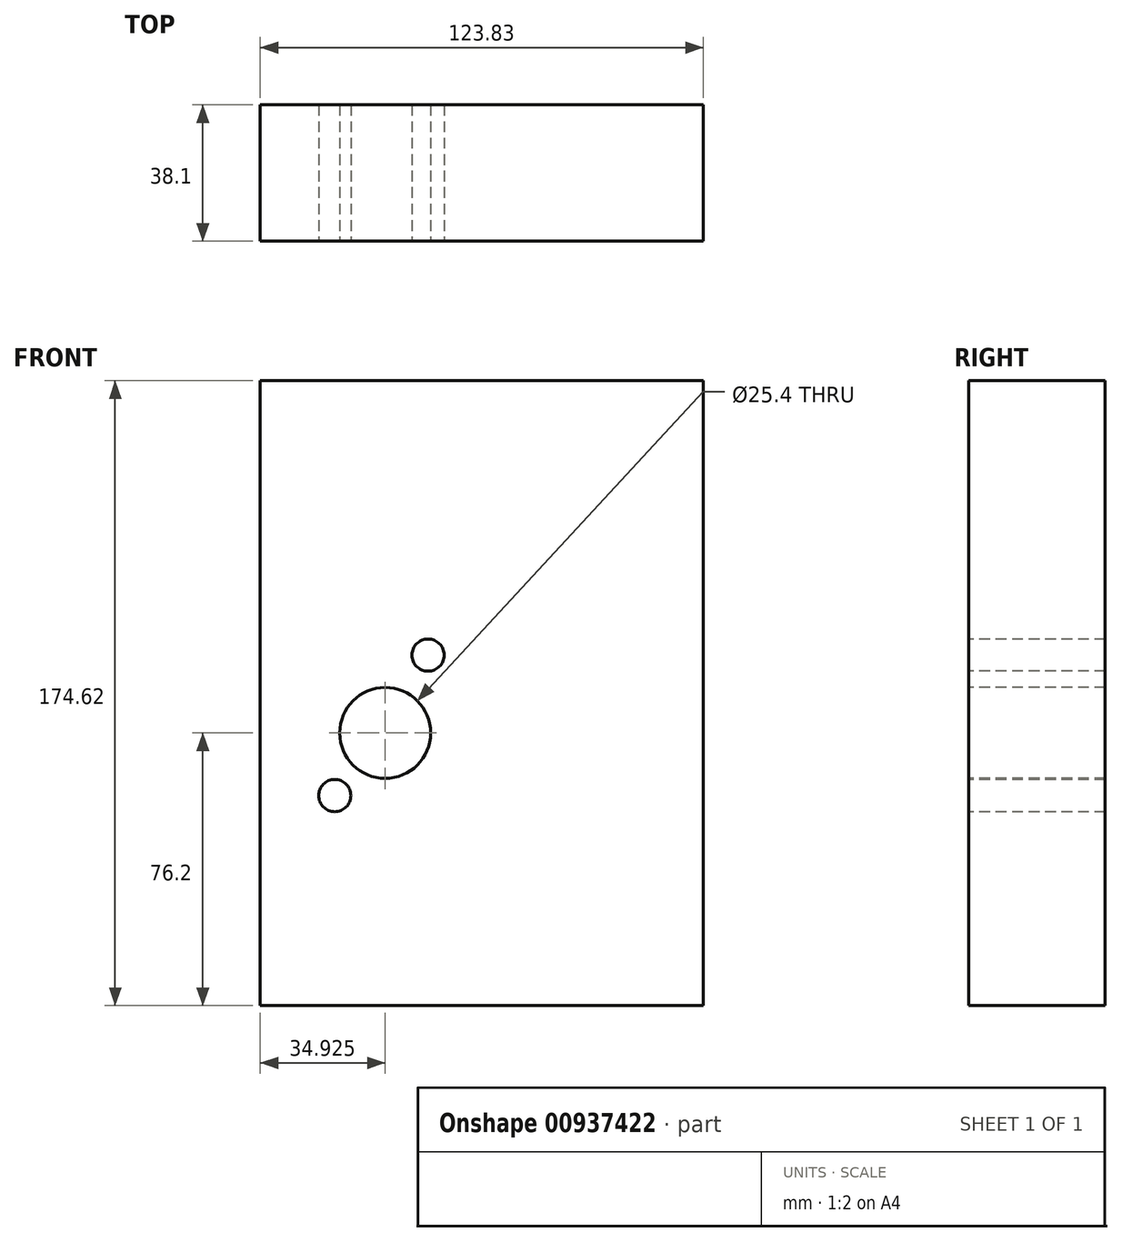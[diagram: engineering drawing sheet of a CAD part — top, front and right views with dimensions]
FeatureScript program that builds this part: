
annotation { "Feature Type Name" : "Feature", "Feature Type Description" : "" }
export const myFeature = defineFeature(function(context is Context, id is Id, definition is map)
    precondition{}
    {
        {
            var Q0;
            Q0=qCreatedBy(makeId("Top.planeOp"),FACE);
            var sketch = newSketch(context, id + "F0", { "sketchPlane" : qUnion([Q0])});
            skLineSegment(sketch, "E0.bottom", {"start": v(0, 0) * mm, "end": v(123.83, 0) * mm});
            skLineSegment(sketch, "E0.top", {"start": v(0, 38.1) * mm, "end": v(123.83, 38.1) * mm});
            skLineSegment(sketch, "E0.left", {"start": v(0, 0) * mm, "end": v(0, 38.1) * mm});
            skLineSegment(sketch, "E0.right", {"start": v(123.83, 0) * mm, "end": v(123.83, 38.1) * mm});
            skSolve(sketch);
        }
        {
            var Q0;
            Q0=makeQuery(id+"F0.imprint","IMPRINT",FACE,{"disambiguationData":[TD([[makeQuery(id+"F0.imprint","IMPRINT",EDGE,{"derivedFrom":sQuery(id+"F0.wireOp",EDGE,"E0.bottom")}),1.0]])]});
            extrude(context, id + "F1", {"entities" : qUnion([Q0]), "depth" : 174.62 * mm, "offsetDistance" : 25.4 * mm});
        }
        {
            var Q0;
            Q0=makeQuery(id+"F1.opExtrude","SWEPT_FACE",FACE,{"disambiguationData":[OSD([sQuery(id+"F0.wireOp",EDGE,"E0.bottom")])]});
            var sketch = newSketch(context, id + "F2", { "sketchPlane" : qUnion([Q0])});
            skCircle(sketch, "E1", {"center": v(34.93, 76.2) * mm, "radius": 12.7 * mm});
            skSolve(sketch);
        }
        {
            var Q0;
            Q0=makeQuery(id+"F2.imprint","IMPRINT",FACE,{"disambiguationData":[TD([[makeQuery(id+"F2.imprint","IMPRINT",EDGE,{"derivedFrom":sQuery(id+"F2.wireOp",EDGE,"E1")}),-1.0]])]});
            var sketch = newSketch(context, id + "F3", { "sketchPlane" : qUnion([Q0])});
            skCircle(sketch, "E2", {"center": v(46.89, 97.96) * mm, "radius": 4.5 * mm});
            skCircle(sketch, "E3", {"center": v(20.84, 58.7) * mm, "radius": 4.5 * mm});
            skSolve(sketch);
        }
        {
            var Q0;
            Q0=makeQuery(id+"F2.imprint","IMPRINT",FACE,{"disambiguationData":[TD([[makeQuery(id+"F2.imprint","IMPRINT",EDGE,{"derivedFrom":sQuery(id+"F2.wireOp",EDGE,"E1")}),1.0]])]});
            var Q1;
            Q1=makeQuery(id+"F3.imprint","IMPRINT",FACE,{"disambiguationData":[TD([[makeQuery(id+"F3.imprint","IMPRINT",EDGE,{"derivedFrom":sQuery(id+"F3.wireOp",EDGE,"E2")}),1.0]])]});
            var Q2;
            Q2=makeQuery(id+"F3.imprint","IMPRINT",FACE,{"disambiguationData":[TD([[makeQuery(id+"F3.imprint","IMPRINT",EDGE,{"derivedFrom":sQuery(id+"F3.wireOp",EDGE,"E3")}),1.0]])]});
            extrude(context, id + "F4", {"entities" : qUnion([Q0, Q1, Q2]), "operationType" : NewBodyOperationType.REMOVE, "endBound" : BoundingType.THROUGH_ALL, "oppositeDirection" : true, "depth" : 25.4 * mm, "offsetDistance" : 25.4 * mm});
        }
    });
